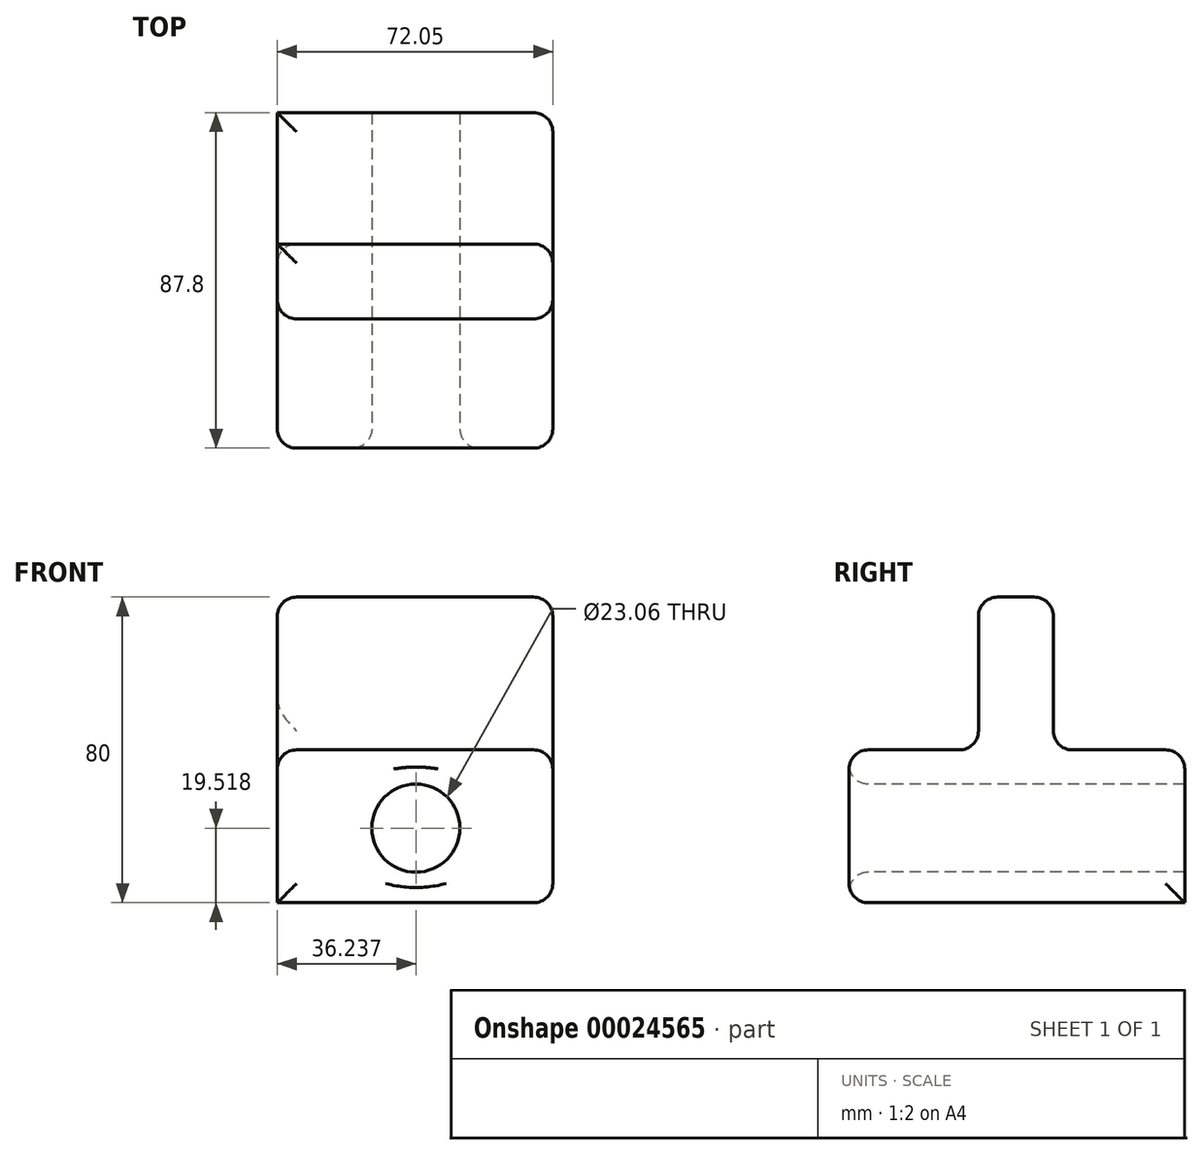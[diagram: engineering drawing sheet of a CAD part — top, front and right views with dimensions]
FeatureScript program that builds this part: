
annotation { "Feature Type Name" : "Feature", "Feature Type Description" : "" }
export const myFeature = defineFeature(function(context is Context, id is Id, definition is map)
    precondition{}
    {
        {
            var Q0;
            Q0=qCreatedBy(makeId("Top.planeOp"),FACE);
            var sketch = newSketch(context, id + "F0", { "sketchPlane" : qUnion([Q0])});
            skLineSegment(sketch, "E0.bottom", {"start": v(-59.89, -44.54) * mm, "end": v(12.16, -44.54) * mm});
            skLineSegment(sketch, "E0.top", {"start": v(-59.89, 43.26) * mm, "end": v(12.16, 43.26) * mm});
            skLineSegment(sketch, "E0.left", {"start": v(-59.89, -44.54) * mm, "end": v(-59.89, 43.26) * mm});
            skLineSegment(sketch, "E0.right", {"start": v(12.16, -44.54) * mm, "end": v(12.16, 43.26) * mm});
            skSolve(sketch);
        }
        {
            var Q0;
            Q0=makeQuery(id+"F0.imprint","IMPRINT",FACE,{"disambiguationData":[TD([[makeQuery(id+"F0.imprint","IMPRINT",EDGE,{"derivedFrom":sQuery(id+"F0.wireOp",EDGE,"E0.bottom")}),1.0]])]});
            extrude(context, id + "F1", {"entities" : qUnion([Q0]), "depth" : 40 * mm});
        }
        {
            var Q0;
            Q0=makeQuery(id+"F1.opExtrude","SWEPT_FACE",FACE,{"disambiguationData":[OSD([sQuery(id+"F0.wireOp",EDGE,"E0.bottom")])]});
            var sketch = newSketch(context, id + "F2", { "sketchPlane" : qUnion([Q0])});
            skCircle(sketch, "E1", {"center": v(-23.65, 19.52) * mm, "radius": 11.53 * mm});
            skSolve(sketch);
        }
        {
            var Q0;
            Q0=makeQuery(id+"F2.imprint","IMPRINT",FACE,{"disambiguationData":[TD([[makeQuery(id+"F2.imprint","IMPRINT",EDGE,{"derivedFrom":sQuery(id+"F2.wireOp",EDGE,"E1")}),1.0]])]});
            extrude(context, id + "F3", {"entities" : qUnion([Q0]), "operationType" : NewBodyOperationType.REMOVE, "endBound" : BoundingType.THROUGH_ALL, "oppositeDirection" : true, "depth" : 25 * mm});
        }
        {
            var Q0;
            Q0=makeQuery(id+"F1.opExtrude","CAP_FACE",FACE,{"disambiguationData":[OSD([sQuery(id+"F0.wireOp",EDGE,"E0.bottom"),sQuery(id+"F0.wireOp",EDGE,"E0.top"),sQuery(id+"F0.wireOp",EDGE,"E0.left"),sQuery(id+"F0.wireOp",EDGE,"E0.right")])],"isStart":false});
            var sketch = newSketch(context, id + "F4", { "sketchPlane" : qUnion([Q0])});
            skLineSegment(sketch, "E2.bottom", {"start": v(-59.89, -10.7) * mm, "end": v(12.16, -10.7) * mm});
            skLineSegment(sketch, "E2.top", {"start": v(-59.89, 8.88) * mm, "end": v(12.16, 8.88) * mm});
            skLineSegment(sketch, "E2.left", {"start": v(-59.89, -10.7) * mm, "end": v(-59.89, 8.88) * mm});
            skLineSegment(sketch, "E2.right", {"start": v(12.16, -10.7) * mm, "end": v(12.16, 8.88) * mm});
            skSolve(sketch);
        }
        {
            var Q0;
            Q0=makeQuery(id+"F4.imprint","IMPRINT",FACE,{"disambiguationData":[TD([[makeQuery(id+"F4.imprint","IMPRINT",EDGE,{"derivedFrom":sQuery(id+"F4.wireOp",EDGE,"E2.bottom")}),1.0]])]});
            extrude(context, id + "F5", {"entities" : qUnion([Q0]), "operationType" : NewBodyOperationType.ADD, "depth" : 40 * mm});
        }
        {
            var Q0;
            Q0=makeQuery(id+"F5.opExtrude","SWEPT_FACE",FACE,{"disambiguationData":[OSD([sQuery(id+"F4.wireOp",EDGE,"E2.bottom")])]});
            var Q1;
            Q1=makeQuery(id+"F5.opExtrude","CAP_FACE",FACE,{"disambiguationData":[OSD([sQuery(id+"F4.wireOp",EDGE,"E2.bottom"),sQuery(id+"F4.wireOp",EDGE,"E2.top"),sQuery(id+"F4.wireOp",EDGE,"E2.left"),sQuery(id+"F4.wireOp",EDGE,"E2.right")])],"isStart":false});
            var Q2;
            Q2=makeQuery(id+"F5.boolean.opBoolean","MERGE",FACE,{"derivedFrom":[makeQuery(id+"F1.opExtrude","SWEPT_FACE",FACE,{"disambiguationData":[OSD([sQuery(id+"F0.wireOp",EDGE,"E0.right")])]}),makeQuery(id+"F5.opExtrude","SWEPT_FACE",FACE,{"disambiguationData":[OSD([sQuery(id+"F4.wireOp",EDGE,"E2.right")])]})]});
            var Q3;
            {var subQ0=sQuery(id+"F0.wireOp",EDGE,"E0.top");var subQ1=sQuery(id+"F0.wireOp",EDGE,"E0.left");var subQ2=sQuery(id+"F0.wireOp",EDGE,"E0.right");Q3=makeQuery(id+"F5.boolean.opBoolean","SPLIT",FACE,{"disambiguationData":[TD([makeQuery(id+"F1.opExtrude","SWEPT_FACE",FACE,{"disambiguationData":[OSD([subQ0])]})])],"derivedFrom":makeQuery(id+"F1.opExtrude","CAP_FACE",FACE,{"disambiguationData":[OSD([sQuery(id+"F0.wireOp",EDGE,"E0.bottom"),subQ0,subQ1,subQ2])],"isStart":false})});}
            var Q4;
            {var subQ0=sQuery(id+"F0.wireOp",EDGE,"E0.bottom");var subQ1=sQuery(id+"F0.wireOp",EDGE,"E0.left");var subQ2=sQuery(id+"F0.wireOp",EDGE,"E0.right");Q4=makeQuery(id+"F5.boolean.opBoolean","SPLIT",FACE,{"disambiguationData":[TD([makeQuery(id+"F1.opExtrude","SWEPT_FACE",FACE,{"disambiguationData":[OSD([subQ0])]})])],"derivedFrom":makeQuery(id+"F1.opExtrude","CAP_FACE",FACE,{"disambiguationData":[OSD([subQ0,sQuery(id+"F0.wireOp",EDGE,"E0.top"),subQ1,subQ2])],"isStart":false})});}
            var Q5;
            Q5=makeQuery(id+"F1.opExtrude","SWEPT_FACE",FACE,{"disambiguationData":[OSD([sQuery(id+"F0.wireOp",EDGE,"E0.bottom")])]});
            fillet(context, id + "F6", {"entities" : qUnion([Q0, Q1, Q2, Q3, Q4, Q5]), "radius" : 5 * mm, "tangentPropagation" : true, "allowEdgeOverflow" : false});
        }
    });
